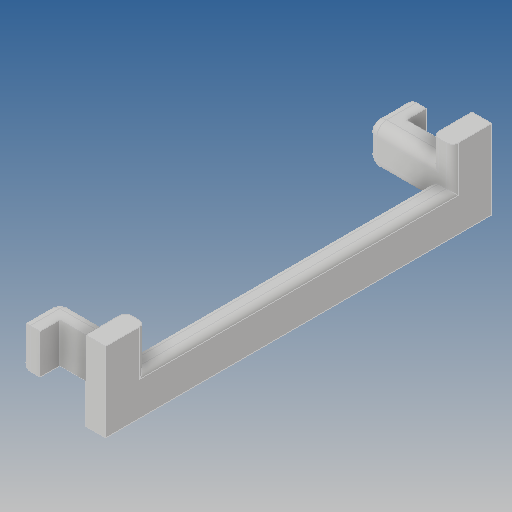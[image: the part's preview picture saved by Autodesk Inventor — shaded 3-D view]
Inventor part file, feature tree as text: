
AUTODESK INVENTOR PART (.ipt)
format: ipt  version: 2020 (Build 240168000, 168)  size: 190,976 bytes
history: native  units: mm
features: extrude x5, sketch x4, fillet x3, projected_geometry x2, other x1, mirror x1
ambient origin geometry x8: Origin, YZ Plane, XZ Plane, XY Plane, X Axis, Y Axis, Z Axis, Center Point
bodies: Body1 (feature_tree)
feature tree (16):
  other  "Твердое тело1"
  sketch  "Эскиз1"
  extrude  "Выдавливание1"  Depth=4.0mm
  extrude  "Выдавливание2"  Depth=19.5mm
  fillet  "Сопряжение1"  Radius=2.0mm
  extrude  "Выдавливание3"  Depth=1.0mm
  extrude  "Выдавливание4"  Depth=2.0mm
  fillet  "Сопряжение2"  Radius=1.0mm
  mirror  "Зеркальное отражение1"
  extrude  "Выдавливание6"  Depth=2.0mm TaperAngle=0.0deg
  fillet  "Сопряжение4"  Radius=1.0mm
  sketch  "Эскиз2"
  projected_geometry  "Спроецированная петля1"
  sketch  "Эскиз3"
  projected_geometry  "Спроецированная петля2"
  sketch  "Эскиз5"
